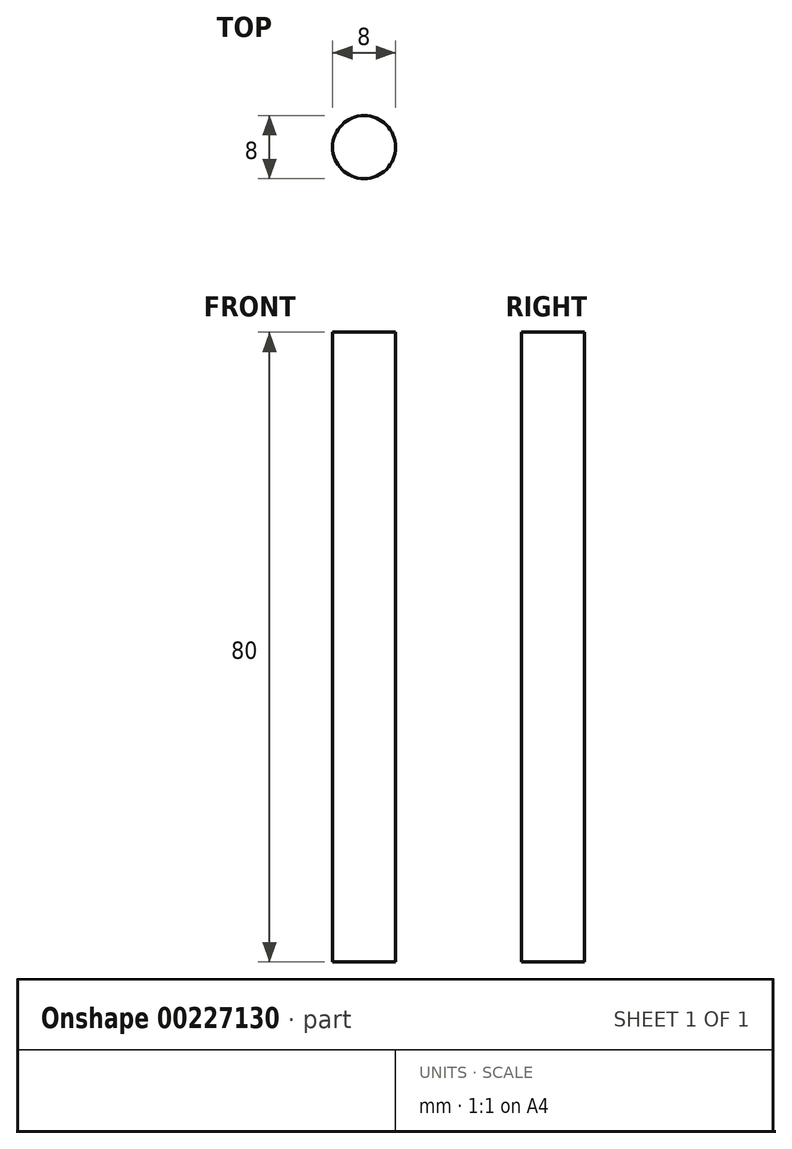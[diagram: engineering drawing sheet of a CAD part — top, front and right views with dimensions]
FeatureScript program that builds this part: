
annotation { "Feature Type Name" : "Feature", "Feature Type Description" : "" }
export const myFeature = defineFeature(function(context is Context, id is Id, definition is map)
    precondition{}
    {
        {
            var Q0;
            Q0=qCreatedBy(makeId("Top.planeOp"),FACE);
            var sketch = newSketch(context, id + "F0", { "sketchPlane" : qUnion([Q0])});
            skCircle(sketch, "E0", {"center": v(0, 0) * mm, "radius": 4 * mm});
            skSolve(sketch);
        }
        {
            var Q0;
            Q0=makeQuery(id+"F0.imprint","IMPRINT",FACE,{"disambiguationData":[TD([[makeQuery(id+"F0.imprint","IMPRINT",EDGE,{"derivedFrom":sQuery(id+"F0.wireOp",EDGE,"E0")}),1.0]])]});
            extrude(context, id + "F1", {"entities" : qUnion([Q0]), "depth" : 80 * mm});
        }
    });
